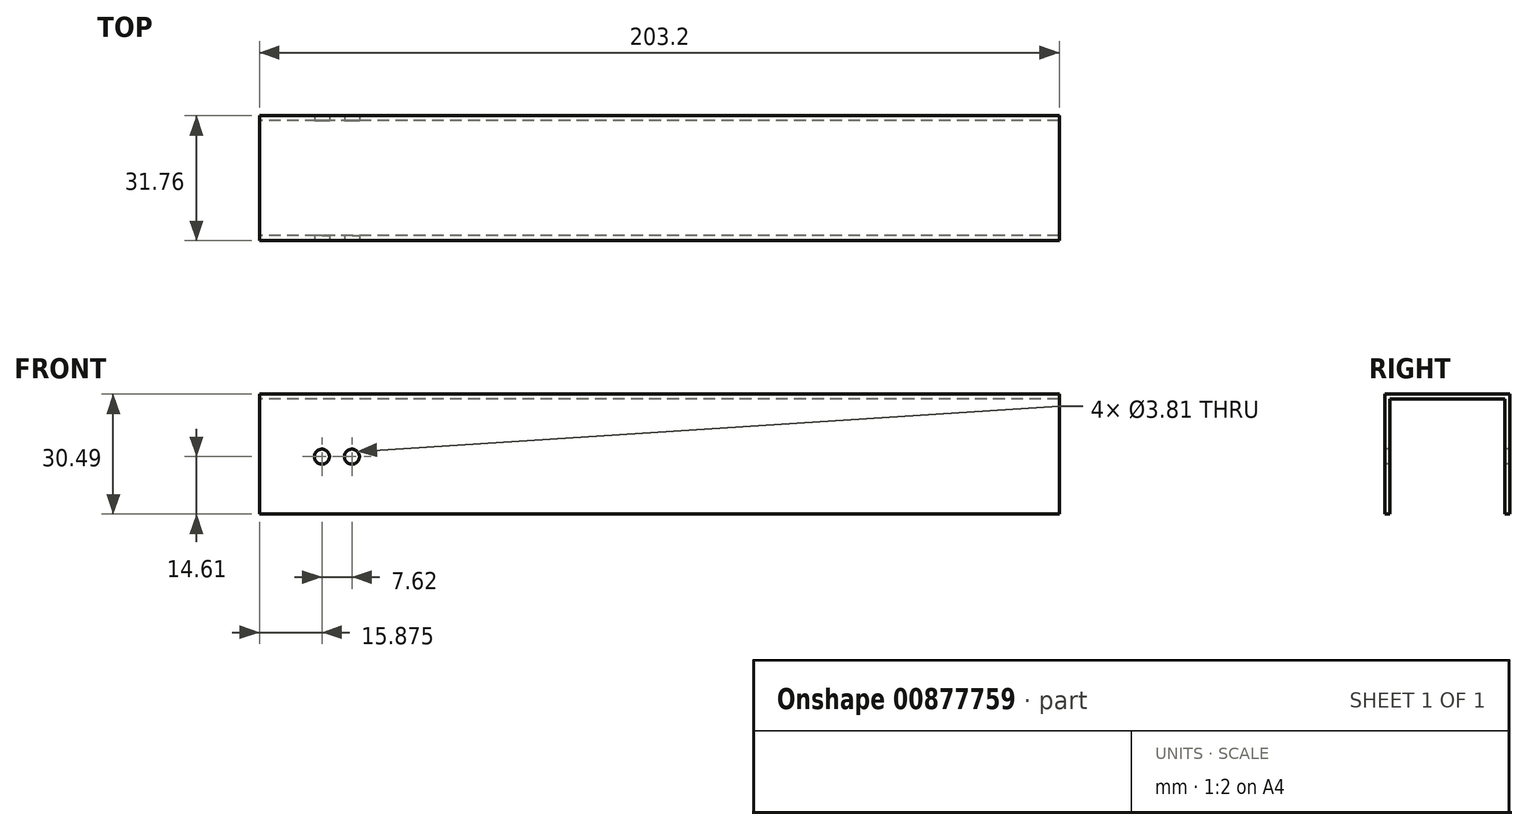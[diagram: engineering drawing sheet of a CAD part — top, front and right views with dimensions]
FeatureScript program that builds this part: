
annotation { "Feature Type Name" : "Feature", "Feature Type Description" : "" }
export const myFeature = defineFeature(function(context is Context, id is Id, definition is map)
    precondition{}
    {
        {
            var Q0;
            Q0=qCreatedBy(makeId("Right.planeOp"),FACE);
            var sketch = newSketch(context, id + "F0", { "sketchPlane" : qUnion([Q0])});
            skLineSegment(sketch, "E0.bottom", {"start": v(15.88, 15.88) * mm, "end": v(-15.88, 15.87) * mm});
            skLineSegment(sketch, "E0.left", {"start": v(15.88, 15.88) * mm, "end": v(15.88, -14.6) * mm});
            skLineSegment(sketch, "E0.right", {"start": v(-15.88, 15.88) * mm, "end": v(-15.88, -14.6) * mm});
            skPoint(sketch, "E0.middle", {"position": v(0, 0) * mm});
            skLineSegment(sketch, "E1.bottom", {"start": v(14.6, 14.6) * mm, "end": v(-14.6, 14.6) * mm});
            skLineSegment(sketch, "E1.left", {"start": v(14.6, 14.6) * mm, "end": v(14.6, -14.6) * mm});
            skLineSegment(sketch, "E1.right", {"start": v(-14.6, 14.6) * mm, "end": v(-14.6, -14.6) * mm});
            skLineSegment(sketch, "E2", {"start": v(14.6, -14.6) * mm, "end": v(15.88, -14.6) * mm});
            skLineSegment(sketch, "E3", {"start": v(15.88, -14.6) * mm, "end": v(14.6, -14.6) * mm});
            skPoint(sketch, "E0.top.start.orphan", {"position": v(15.88, -15.87) * mm});
            skLineSegment(sketch, "E4", {"start": v(-14.6, -14.6) * mm, "end": v(-15.88, -14.6) * mm});
            skPoint(sketch, "E5.orphan", {"position": v(-15.88, -15.88) * mm});
            skSolve(sketch);
        }
        {
            var Q0;
            Q0 = qSketchRegion(id + "F0", true);
            extrude(context, id + "F1", {"entities" : qUnion([Q0]), "depth" : 203.2 * mm, "offsetDistance" : 25.4 * mm});
        }
        {
            var Q0;
            Q0=makeQuery(id+"F1.opExtrude","SWEPT_FACE",FACE,{"disambiguationData":[OSD([sQuery(id+"F0.wireOp",EDGE,"E0.right")])]});
            var sketch = newSketch(context, id + "F2", { "sketchPlane" : qUnion([Q0])});
            skCircle(sketch, "E6", {"center": v(15.88, 0) * mm, "radius": 1.9 * mm});
            skCircle(sketch, "E7", {"center": v(23.5, 0) * mm, "radius": 1.9 * mm});
            skSolve(sketch);
        }
        {
            var Q0;
            Q0 = qSketchRegion(id + "F2", true);
            extrude(context, id + "F3", {"entities" : qUnion([Q0]), "operationType" : NewBodyOperationType.REMOVE, "endBound" : BoundingType.THROUGH_ALL, "oppositeDirection" : true, "depth" : 25.4 * mm, "offsetDistance" : 25.4 * mm});
        }
    });
